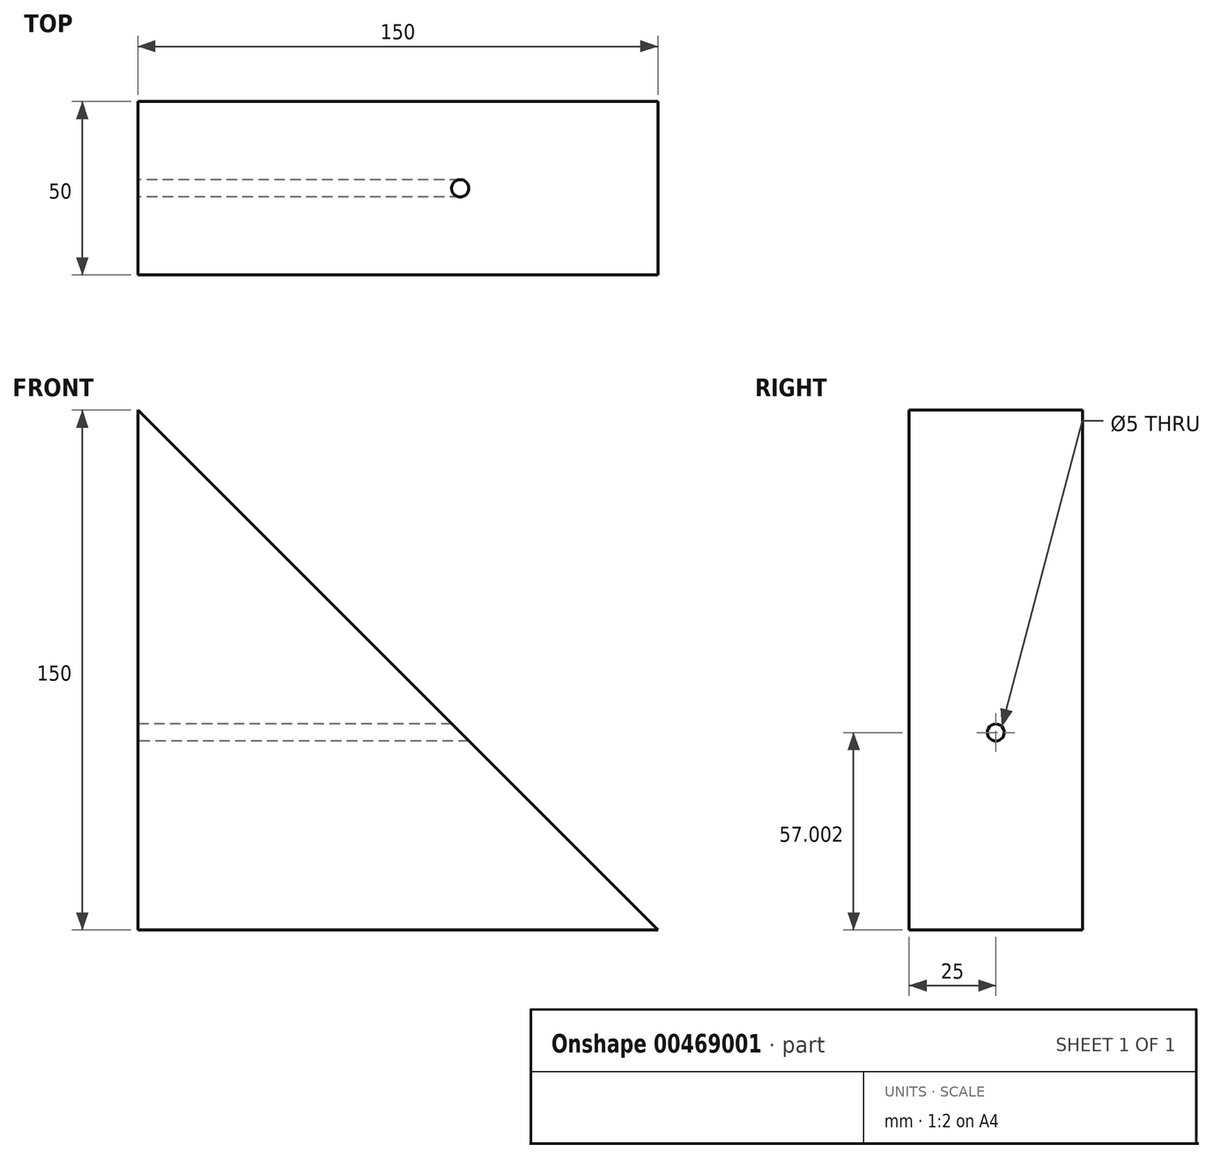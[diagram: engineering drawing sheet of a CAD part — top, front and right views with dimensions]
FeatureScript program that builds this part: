
annotation { "Feature Type Name" : "Feature", "Feature Type Description" : "" }
export const myFeature = defineFeature(function(context is Context, id is Id, definition is map)
    precondition{}
    {
        {
            var Q0;
            Q0=qCreatedBy(makeId("Front.planeOp"),FACE);
            var sketch = newSketch(context, id + "F0", { "sketchPlane" : qUnion([Q0])});
            skLineSegment(sketch, "E0.top", {"start": v(0, 1.11) * mm, "end": v(150, 1.11) * mm});
            skLineSegment(sketch, "E0.right", {"start": v(150, 151.11) * mm, "end": v(150, 1.11) * mm});
            skLineSegment(sketch, "E1", {"start": v(0, 1.11) * mm, "end": v(150, 151.11) * mm});
            skPoint(sketch, "E0.left.start.orphan", {"position": v(0, 151.11) * mm});
            skSolve(sketch);
        }
        {
            var Q0;
            Q0=makeQuery(id+"F0.imprint","IMPRINT",FACE,{"disambiguationData":[TD([[makeQuery(id+"F0.imprint","IMPRINT",EDGE,{"derivedFrom":sQuery(id+"F0.wireOp",EDGE,"E0.top")}),1.0]])]});
            var Q1;
            Q1 = qSketchRegion(id + "FFATL44v5OtHZws_1", true);
            extrude(context, id + "F1", {"entities" : qUnion([Q0, Q1]), "depth" : 50 * mm});
        }
        {
            var Q0;
            Q0=makeQuery(id+"F1.opExtrude","SWEPT_BODY",BODY,{"disambiguationData":[OSD([sQuery(id+"F0.wireOp",EDGE,"E0.top"),sQuery(id+"F0.wireOp",EDGE,"E0.right"),sQuery(id+"F0.wireOp",EDGE,"E1")])]});
            var Q1;
            Q1=qCreatedBy(makeId("Right.planeOp"),FACE);
            mirror(context, id + "F2", {"operationType" : NewBodyOperationType.ADD, "entities" : qUnion([Q0]), "mirrorPlane" : qUnion([Q1])});
        }
        {
            var Q0;
            Q0=makeQuery(id+"F1.opExtrude","SWEPT_BODY",BODY,{"disambiguationData":[OSD([sQuery(id+"F0.wireOp",EDGE,"E0.top"),sQuery(id+"F0.wireOp",EDGE,"E0.right"),sQuery(id+"F0.wireOp",EDGE,"E1")])]});
            deleteBodies(context, id + "F3", {"entities" : qUnion([Q0])});
        }
        {
            var Q0;
            Q0=makeQuery(id+"F2.opPattern","COPY",FACE,{"derivedFrom":makeQuery(id+"F1.opExtrude","SWEPT_FACE",FACE,{"disambiguationData":[OSD([sQuery(id+"F0.wireOp",EDGE,"E0.right")])]}),"instanceName":"1"});
            var sketch = newSketch(context, id + "F4", { "sketchPlane" : qUnion([Q0])});
            skCircle(sketch, "E2", {"center": v(25, 58.11) * mm, "radius": 2.5 * mm});
            skPoint(sketch, "E2.centerSnap0", {"position": v(25, 1.11) * mm});
            skSolve(sketch);
        }
        {
            var Q0;
            Q0 = qSketchRegion(id + "F4", true);
            extrude(context, id + "F5", {"entities" : qUnion([Q0]), "operationType" : NewBodyOperationType.REMOVE, "endBound" : BoundingType.THROUGH_ALL, "oppositeDirection" : true, "depth" : 25 * mm});
        }
    });
